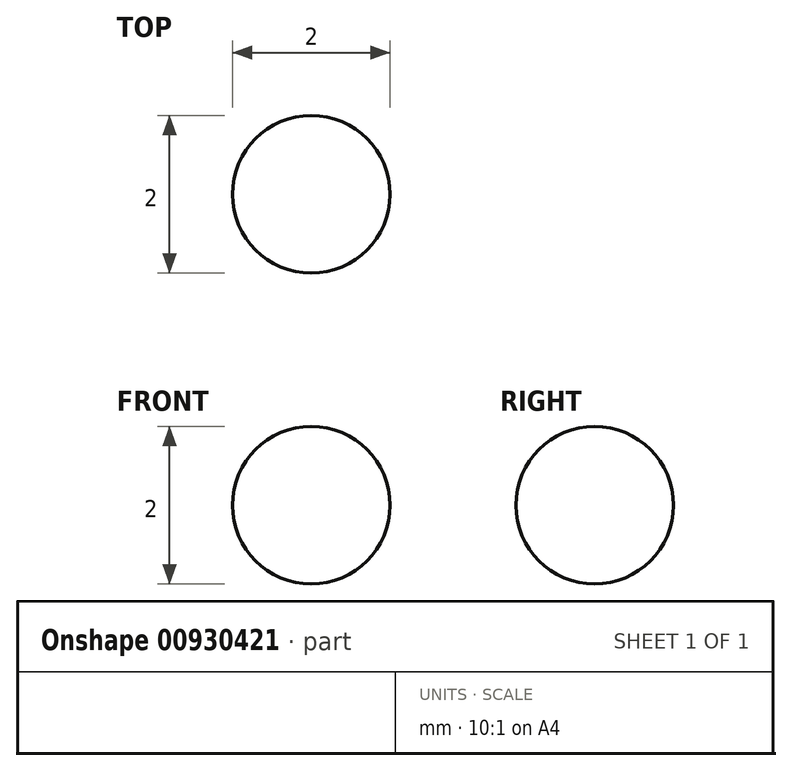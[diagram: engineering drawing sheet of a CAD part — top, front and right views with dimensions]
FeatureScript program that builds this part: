
annotation { "Feature Type Name" : "Feature", "Feature Type Description" : "" }
export const myFeature = defineFeature(function(context is Context, id is Id, definition is map)
    precondition{}
    {
        {
            var Q0;
            Q0=qCreatedBy(makeId("Top.planeOp"),FACE);
            var sketch = newSketch(context, id + "F0", { "sketchPlane" : qUnion([Q0])});
            skArc(sketch, "E0", {"start": v(6, 0) * mm, "mid": v(7, 1) * mm, "end": v(8, 0) * mm});
            skLineSegment(sketch, "E1", {"start": v(6, 0) * mm, "end": v(8, 0) * mm});
            skSolve(sketch);
        }
        {
            var Q0;
            Q0 = qSketchRegion(id + "F0", true);
            var Q1;
            Q1=sQuery(id+"F0.wireOp",EDGE,"E1");
            revolve(context, id + "F1", {"surfaceOperationType" : NewSurfaceOperationType.NEW, "entities" : qUnion([Q0]), "axis" : qUnion([Q1]), "revolveType" : RevolveType.FULL});
        }
    });
